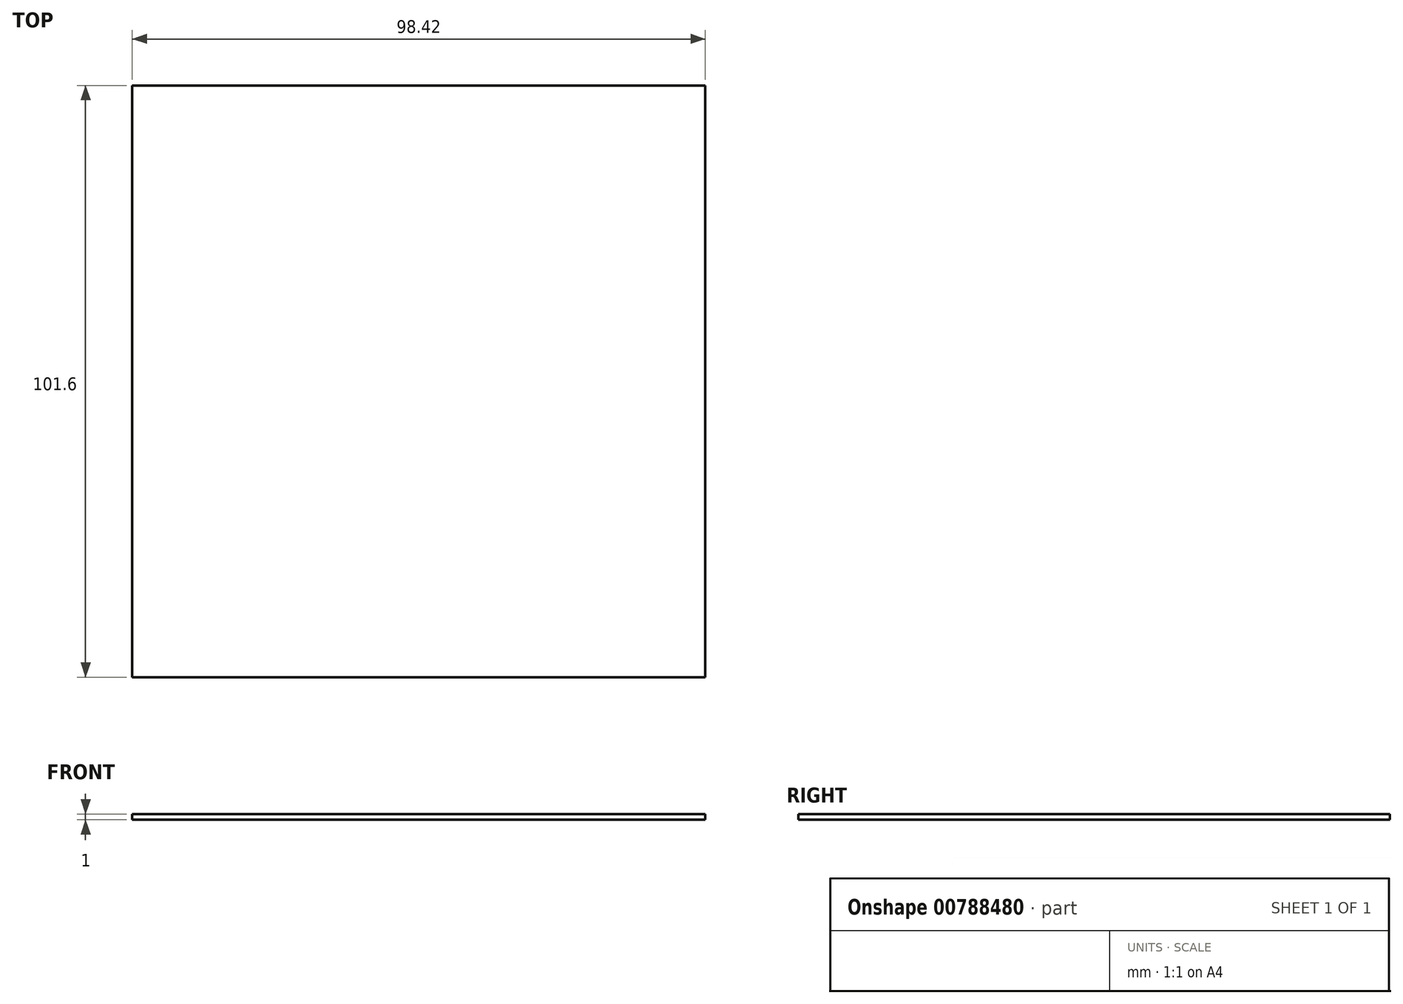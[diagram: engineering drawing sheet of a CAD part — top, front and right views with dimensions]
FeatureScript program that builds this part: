
annotation { "Feature Type Name" : "Feature", "Feature Type Description" : "" }
export const myFeature = defineFeature(function(context is Context, id is Id, definition is map)
    precondition{}
    {
        {
            assignVariable(context, id + "F0", {"name" : "H", "anyValue" : 1});
        }
        {
            var Q0;
            Q0=qCreatedBy(makeId("Top.planeOp"),FACE);
            var sketch = newSketch(context, id + "F1", { "sketchPlane" : qUnion([Q0])});
            skLineSegment(sketch, "E0.bottom", {"start": v(-49.21, 50.8) * mm, "end": v(49.21, 50.8) * mm});
            skLineSegment(sketch, "E0.top", {"start": v(-49.21, -50.8) * mm, "end": v(49.21, -50.8) * mm});
            skLineSegment(sketch, "E0.left", {"start": v(-49.21, 50.8) * mm, "end": v(-49.21, -50.8) * mm});
            skLineSegment(sketch, "E0.right", {"start": v(49.21, 50.8) * mm, "end": v(49.21, -50.8) * mm});
            skPoint(sketch, "E1", {"position": v(-76.2, 50.8) * mm});
            skPoint(sketch, "E2.MirrorP", {"position": v(76.2, 50.8) * mm});
            skSolve(sketch);
        }
        {
            var Q0;
            Q0=qSketchRegion(id+"F1",true);
            extrude(context, id + "F2", {"entities" : qUnion([Q0]), "depth" : (getVariable(context, 'H')) * mm});
        }
    });
